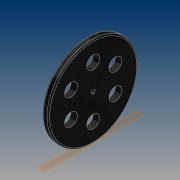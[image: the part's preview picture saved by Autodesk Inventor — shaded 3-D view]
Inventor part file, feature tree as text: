
AUTODESK INVENTOR PART (.ipt)
format: ipt  version: 2021 (Build 250183000, 183)  size: 139,776 bytes
history: native  units: mm
features: extrude x2, sketch x2, fillet x1, pattern_circular x1, plane x1
ambient origin geometry x8: Origin, YZ Plane, XZ Plane, XY Plane, X Axis, Y Axis, Z Axis, Center Point
bodies: Solid1 (feature_tree)
feature tree (7):
  extrude  "Extrusion1"  Depth=10.0mm
  fillet  "Fillet1"  Radius=10.0mm
  extrude  "Extrusion2"  Depth=10.0mm
  pattern_circular  "Circular Pattern1"  Count=4  [1 undecoded]
  plane  "Work Plane1"
  sketch  "Sketch1"  dims[d0=140.0mm d1=6.0mm d2=10.0mm d3=0.0mm]
  sketch  "Sketch2"  dims[d4=2.0mm d5=20.0mm d6=40.0mm d7=10.0mm d8=0.0mm d9=60.0mm d10=360.0deg]
note: 1 required parameter value undecoded (feature->parameter linkage not recoverable at this tier; creation-order binding heuristic only, values carry confidence <= 0.55)
